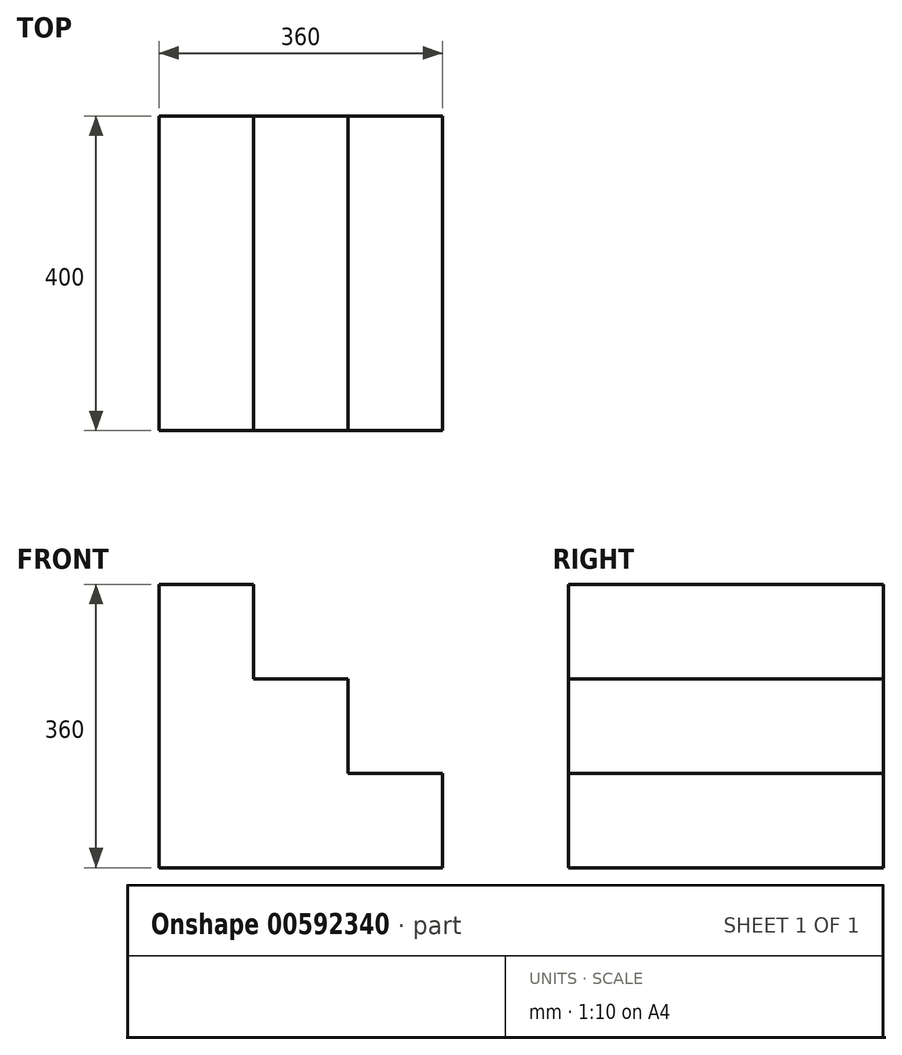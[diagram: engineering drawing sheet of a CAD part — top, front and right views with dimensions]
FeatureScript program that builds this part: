
annotation { "Feature Type Name" : "Feature", "Feature Type Description" : "" }
export const myFeature = defineFeature(function(context is Context, id is Id, definition is map)
    precondition{}
    {
        {
            var Q0;
            Q0=qCreatedBy(makeId("Front.planeOp"),FACE);
            var sketch = newSketch(context, id + "F0", { "sketchPlane" : qUnion([Q0])});
            skLineSegment(sketch, "E0", {"start": v(0, 0) * mm, "end": v(-360, 0) * mm});
            skLineSegment(sketch, "E1", {"start": v(-360, 0) * mm, "end": v(-360, 360) * mm});
            skLineSegment(sketch, "E2", {"start": v(-360, 360) * mm, "end": v(-240, 360) * mm});
            skLineSegment(sketch, "E3", {"start": v(-240, 360) * mm, "end": v(-240, 240) * mm});
            skLineSegment(sketch, "E4", {"start": v(-240, 240) * mm, "end": v(-120, 240) * mm});
            skLineSegment(sketch, "E5", {"start": v(-120, 240) * mm, "end": v(-120, 120) * mm});
            skLineSegment(sketch, "E6", {"start": v(-120, 120) * mm, "end": v(0, 120) * mm});
            skLineSegment(sketch, "E7", {"start": v(0, 120) * mm, "end": v(0, 0) * mm});
            skSolve(sketch);
        }
        {
            var Q0;
            Q0 = qSketchRegion(id + "F0", true);
            extrude(context, id + "F1", {"entities" : qUnion([Q0]), "depth" : 400 * mm, "offsetDistance" : 25 * mm});
        }
    });
